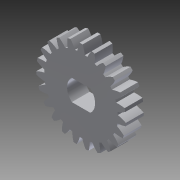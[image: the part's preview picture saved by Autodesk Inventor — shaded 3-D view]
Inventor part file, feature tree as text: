
AUTODESK INVENTOR PART (.ipt)
format: ipt  version: 2014 SP1 (Build 180222100, 222)  size: 256,512 bytes
history: native  units: mm (DEFAULTED — no unit token found)
features: plane x3, other x3, sketch x3, extrude x2
ambient origin geometry x8: Origin, YZ Plane, XZ Plane, XY Plane, X Axis, Y Axis, Z Axis, Center Point
bodies: Solid1 (feature_tree)
feature tree (11):
  extrude  "Extrusion1"  Depth=6.35mm TaperAngle=0.0deg
  plane  "Work Plane1"
  plane  "Work Plane2"
  plane  "Work Plane3"
  other  "Spur Gear"
  extrude  "Extrusion2"  Depth=76.2mm TaperAngle=0.0deg
  sketch  "Sketch1"  dims[d0=31.90875mm d1=6.35mm d2=0.0mm]
  sketch  "Sketch2"  dims[d3=29.21mm d4=76.2mm d5=0.0mm]
  other  "Srf1"
  sketch  "Sketch3"  dims[d6=0.0mm d7=1.36591mm d9=0.0mm d14=0.0mm d15=304.8mm d16=0.0mm d17=0.0mm d18=0.0mm d19=304.8mm d20=25.4mm d21=0.0mm]
  other  "Pitch Diameter"
